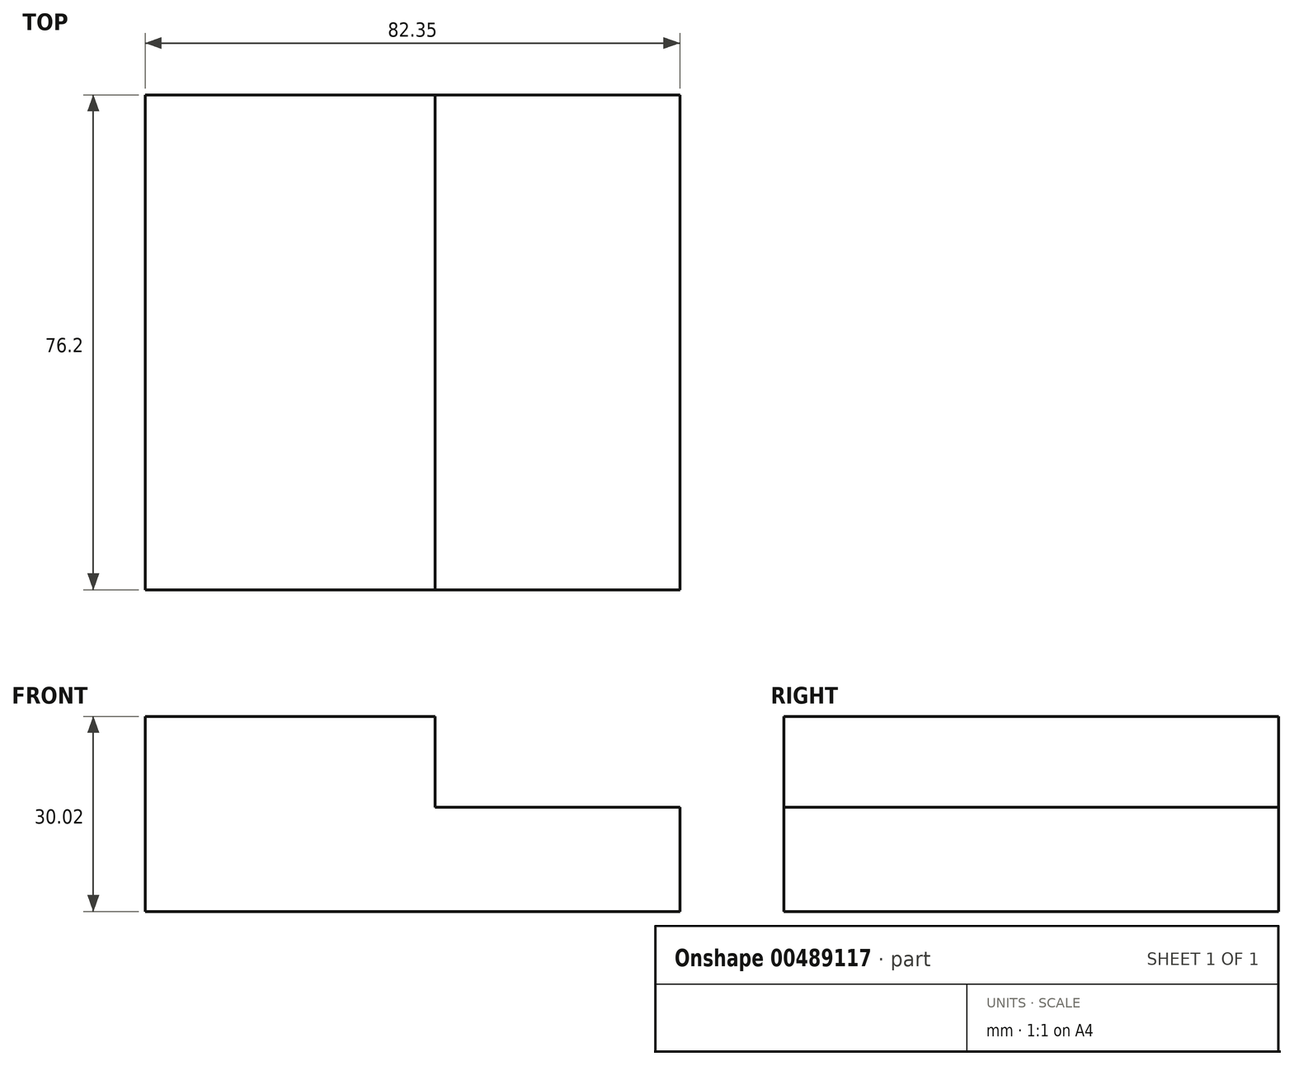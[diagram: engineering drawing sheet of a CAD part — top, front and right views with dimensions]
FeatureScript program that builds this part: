
annotation { "Feature Type Name" : "Feature", "Feature Type Description" : "" }
export const myFeature = defineFeature(function(context is Context, id is Id, definition is map)
    precondition{}
    {
        {
            var Q0;
            Q0=qCreatedBy(makeId("Front.planeOp"),FACE);
            var sketch = newSketch(context, id + "F0", { "sketchPlane" : qUnion([Q0])});
            skLineSegment(sketch, "E0", {"start": v(-58.96, 49.78) * mm, "end": v(-14.3, 49.78) * mm});
            skLineSegment(sketch, "E1", {"start": v(-14.3, 49.78) * mm, "end": v(-14.3, 35.83) * mm});
            skLineSegment(sketch, "E2", {"start": v(-14.3, 35.83) * mm, "end": v(23.39, 35.83) * mm});
            skLineSegment(sketch, "E3", {"start": v(23.39, 35.83) * mm, "end": v(23.39, 19.76) * mm});
            skLineSegment(sketch, "E4", {"start": v(23.39, 19.76) * mm, "end": v(-58.96, 19.76) * mm});
            skLineSegment(sketch, "E5", {"start": v(-58.96, 19.76) * mm, "end": v(-58.96, 49.78) * mm});
            skSolve(sketch);
        }
        {
            var Q0;
            Q0 = qSketchRegion(id + "F0", true);
            extrude(context, id + "F1", {"entities" : qUnion([Q0]), "depth" : 76.2 * mm});
        }
    });
